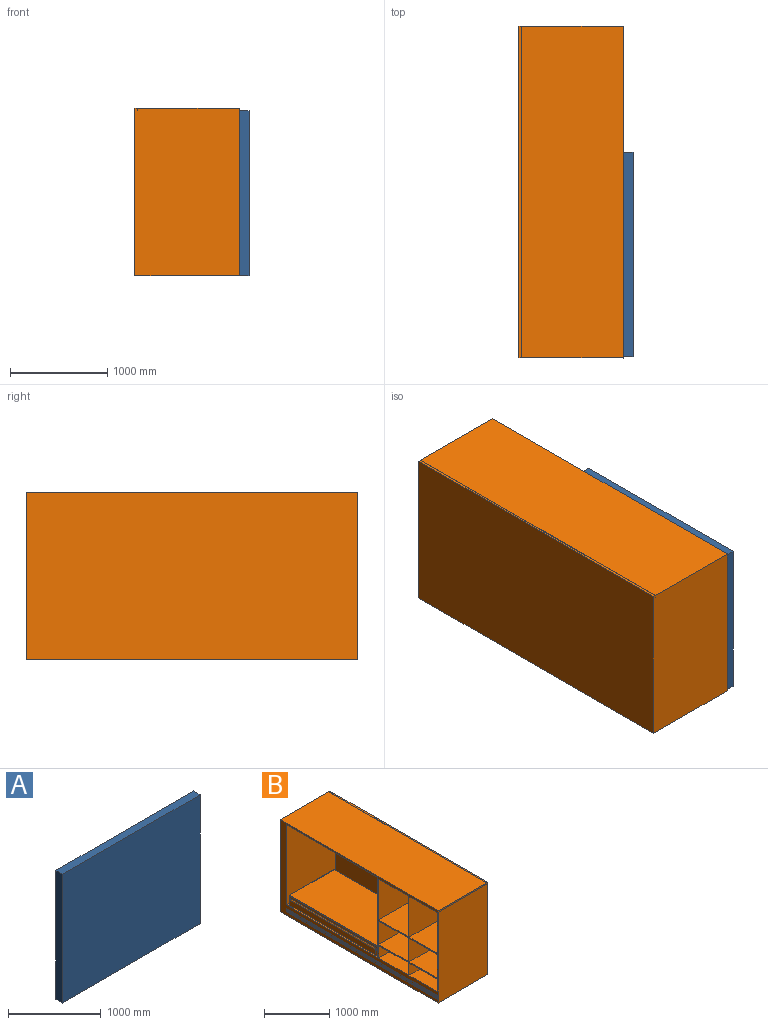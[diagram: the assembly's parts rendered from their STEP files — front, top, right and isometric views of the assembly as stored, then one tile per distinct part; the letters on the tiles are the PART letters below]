
ASSEMBLY  parts=2 mates=2
PART A: 6 faces, bbox 2100x100x1700 mm
  f0: plane 2100x1700mm, normal (0,1,0), area 3570000mm2, adj f1,f3,f4,f5
  f1: plane 1700x100mm, normal (-1,0,0), area 170000mm2, adj f0,f2,f4,f5
  f2: plane 2100x1700mm, normal (0,-1,0), area 3570000mm2, adj f1,f3,f4,f5
  f3: plane 1700x100mm, normal (1,0,0), area 170000mm2, adj f0,f2,f4,f5
  f4: plane 2100x100mm, normal (0,0,1), area 210000mm2, adj f0,f1,f2,f3
  f5: plane 2100x100mm, normal (0,0,-1), area 210000mm2, adj f0,f1,f2,f3
PART B: 94 faces, bbox 1080x3415.1x1725 mm
  f0: plane 763.79x630mm, normal (-1,0,0), area 481187.5mm2, adj f71,f73,f74,f93
  f1: plane 1019x763.79mm, normal (0,1,0), area 775969.2mm2, adj f2,f13,f79,f84,f90
  f2: plane 763.79x610mm, normal (-1,0,0), area 465911.7mm2, adj f1,f76,f79,f90
  f3: plane 1019x441.31mm, normal (0,-1,0), area 449692.9mm2, adj f6,f13,f88,f92
  f4: plane 1019x441.31mm, normal (0,1,0), area 449692.9mm2, adj f6,f13,f88,f92
  f5: plane 1019x441.31mm, normal (0,-1,0), area 449692.9mm2, adj f8,f13,f86,f91
  f6: plane 630x441.31mm, normal (-1,0,0), area 278024.1mm2, adj f3,f4,f88,f92
  f7: plane 1019x441.31mm, normal (0,1,0), area 449692.9mm2, adj f8,f13,f86,f91
  f8: plane 610x441.31mm, normal (-1,0,0), area 269197.9mm2, adj f5,f7,f86,f91
  f9: plane 1019x232.38mm, normal (0,-1,0), area 236797.7mm2, adj f13,f72,f75,f89
  f10: plane 1019x232.38mm, normal (0,1,0), area 236797.7mm2, adj f13,f72,f75,f89
  f11: plane 1019x232.38mm, normal (0,-1,0), area 236797.7mm2, adj f13,f77,f80,f87
  f12: plane 137x1.45mm, normal (0,0,1), area 198.3mm2, adj f15,f19,f20,f83
  f13: plane 3415.14x1725mm, normal (-1,0,0), area 1088941.3mm2, adj f1,f3,f4,f5,f7,f9,f10,f11
  f14: plane 3415.14x1075mm, normal (0,0,-1), area 3671270.9mm2, adj f13,f18,f69,f83
  f15: plane 3414.78x25mm, normal (1,0,0), area 85369.5mm2, adj f12,f16,f21,f81,f82,f83
  f16: plane 3414.78x1048.55mm, normal (0,0,1), area 3580578.9mm2, adj f13,f15,f81,f83
  f17: plane 3415.14x25mm, normal (0,0,1), area 85378.4mm2, adj f18,f19,f69,f83
  f18: plane 3415.14x1724.51mm, normal (1,0,0), area 5889440.8mm2, adj f14,f17,f69,f83
  f19: plane 3415.14x1524.51mm, normal (-1,0,0), area 3050913.7mm2, adj f12,f17,f20,f21,f22,f69,f70,f83
  f20: plane 1500x1050mm, normal (0,-1,0), area 1575000mm2, adj f12,f13,f19,f22,f82
  f21: plane 1300x1050mm, normal (0,0,1), area 2252.7mm2, adj f13,f15,f19,f69,f70,f81
  f22: plane 1978.14x1050mm, normal (0,0,1), area 123979.4mm2, adj f13,f19,f20,f23,f24,f25,f26,f27
  f23: plane 1855.15x100mm, normal (-1,0,0), area 185514.7mm2, adj f22,f27,f30,f36
  f24: plane 905.15x100mm, normal (0,-1,0), area 90514.7mm2, adj f22,f27,f28,f37
  f25: plane 1855.15x100mm, normal (1,0,0), area 185514.7mm2, adj f22,f28,f29,f33
  f26: plane 905.15x100mm, normal (0,1,0), area 90514.7mm2, adj f22,f29,f30,f32
  f27: cylinder r=48.28mm len=100mm, axis (0,0,-1), area 7584.5mm2, adj f22,f23,f24,f38
  f28: cylinder r=48.28mm len=100mm, axis (0,0,1), area 7584.5mm2, adj f22,f24,f25,f35
  f29: cylinder r=48.28mm len=100mm, axis (0,0,-1), area 7584.5mm2, adj f22,f25,f26,f31
  f30: cylinder r=48.28mm len=100mm, axis (0,0,1), area 7584.5mm2, adj f22,f23,f26,f34
  f31: torus R=28.28mm, axis (0,0,1), area 2024.1mm2, adj f29,f32,f33,f39
  f32: cylinder r=20mm len=905.15mm, axis (1,0,0), area 28436mm2, adj f26,f31,f34,f39
  f33: cylinder r=20mm len=1855.15mm, axis (0,-1,0), area 58281.2mm2, adj f25,f31,f35,f39
  f34: torus R=28.28mm, axis (0,0,1), area 2024.1mm2, adj f30,f32,f36,f39
  f35: torus R=28.28mm, axis (0,0,1), area 2024.1mm2, adj f28,f33,f37,f39
  f36: cylinder r=20mm len=1855.15mm, axis (0,1,0), area 58281.2mm2, adj f23,f34,f38,f39
  f37: cylinder r=20mm len=905.15mm, axis (-1,0,0), area 28436mm2, adj f24,f35,f38,f39
  f38: torus R=28.28mm, axis (0,0,1), area 2024.1mm2, adj f27,f36,f37,f39
  f39: plane 1923.48x973.41mm, normal (0,0,-1), area 34400.8mm2, adj f31,f32,f33,f34,f35,f36,f37,f38
  f40: plane 1903.48x40mm, normal (-1,0,0), area 76139.3mm2, adj f39,f45,f48,f54
  f41: plane 953.41x40mm, normal (0,-1,0), area 38136.2mm2, adj f39,f45,f46,f55
  f42: plane 1903.48x40mm, normal (1,0,0), area 76139.3mm2, adj f39,f46,f47,f51
  f43: plane 953.41x40mm, normal (0,1,0), area 38136.2mm2, adj f39,f47,f48,f50
  f44: plane 1903.48x953.41mm, normal (0,0,1), area 1814789.2mm2, adj f50,f51,f54,f55
  f45: cylinder r=10mm len=40mm, axis (0,0,-1), area 628.3mm2, adj f39,f40,f41,f56
  f46: cylinder r=10mm len=40mm, axis (0,0,1), area 628.3mm2, adj f39,f41,f42,f53
  f47: cylinder r=10mm len=40mm, axis (0,0,-1), area 628.3mm2, adj f39,f42,f43,f49
  f48: cylinder r=10mm len=40mm, axis (0,0,1), area 628.3mm2, adj f39,f40,f43,f52
  f49: sphere r=10mm, area 157.1mm2, adj f47,f50,f51
  f50: cylinder r=10mm len=953.41mm, axis (1,0,0), area 14976.1mm2, adj f43,f44,f49,f52
  f51: cylinder r=10mm len=1903.48mm, axis (0,-1,0), area 29899.8mm2, adj f42,f44,f49,f53
  f52: sphere r=10mm, area 157.1mm2, adj f48,f50,f54
  f53: sphere r=10mm, area 157.1mm2, adj f46,f51,f55
  f54: cylinder r=10mm len=1903.48mm, axis (0,1,0), area 29899.8mm2, adj f40,f44,f52,f56
  f55: cylinder r=10mm len=953.41mm, axis (-1,0,0), area 14976.1mm2, adj f41,f44,f53,f56
  f56: sphere r=10mm, area 157.1mm2, adj f45,f54,f55
  f57: plane 3280x5mm, normal (0,0,1), area 16400mm2, adj f13,f58,f60,f69
  f58: plane 5x5mm, normal (0,1,0), area 25mm2, adj f13,f57,f59,f60
  f59: plane 3280x5mm, normal (0,0,-1), area 16400mm2, adj f13,f58,f60,f69
  f60: plane 3280x5mm, normal (-1,0,0), area 16400mm2, adj f57,f58,f59,f69
  f61: plane 3280x5mm, normal (0,0,-1), area 16400mm2, adj f13,f63,f64,f69
  f62: plane 3280x5mm, normal (0,0,1), area 16400mm2, adj f13,f63,f64,f69
  f63: plane 5x5mm, normal (0,1,0), area 25mm2, adj f13,f61,f62,f64
  f64: plane 3280x5mm, normal (-1,0,0), area 16400mm2, adj f61,f62,f63,f69
  f65: plane 3280x5mm, normal (0,0,1), area 16400mm2, adj f13,f66,f68,f69
  f66: plane 6x5mm, normal (0,1,0), area 30mm2, adj f13,f65,f67,f68
  f67: plane 3280x5mm, normal (0,0,-1), area 16400mm2, adj f13,f66,f68,f69
  f68: plane 3280x6mm, normal (-1,0,0), area 19680mm2, adj f65,f66,f67,f69
  f69: plane 1724.51x1080mm, normal (0,-1,0), area 1828192.8mm2, adj f13,f14,f17,f18,f19,f21,f57,f59
  f70: plane 1500x1050mm, normal (0,1,0), area 1575000mm2, adj f13,f19,f21,f22,f82
  f71: plane 1019x763.79mm, normal (0,-1,0), area 775969.2mm2, adj f0,f13,f74,f85,f93
  f72: plane 1019x630mm, normal (0,0,1), area 641970mm2, adj f9,f10,f13,f75
  f73: plane 1019x763.79mm, normal (0,1,0), area 775969.2mm2, adj f0,f13,f74,f85,f93
  f74: plane 1019x630mm, normal (0,0,-1), area 641970mm2, adj f0,f13,f71,f73
  f75: plane 630x232.38mm, normal (-1,0,0), area 146400.9mm2, adj f9,f10,f72,f89
  f76: plane 1019x763.79mm, normal (0,-1,0), area 775969.2mm2, adj f2,f13,f79,f84,f90
  f77: plane 1019x610mm, normal (0,0,1), area 621590mm2, adj f11,f13,f78,f80
  f78: plane 1019x232.38mm, normal (0,1,0), area 236797.7mm2, adj f13,f77,f80,f87
  f79: plane 1019x610mm, normal (0,0,-1), area 621590mm2, adj f1,f2,f13,f76
  f80: plane 610x232.38mm, normal (-1,0,0), area 141753.3mm2, adj f11,f77,f78,f87
  f81: plane 1048.55x25mm, normal (0,-1,0), area 26213.8mm2, adj f13,f15,f16,f21
  f82: plane 1978.14x1048.55mm, normal (0,0,-1), area 2074179.9mm2, adj f13,f15,f20,f70
  f83: plane 1725x1075mm, normal (0,1,0), area 1854326.6mm2, adj f12,f13,f14,f15,f16,f17,f18,f19
  f84: cylinder r=27.25mm len=610mm, axis (0,-1,0), area 104433.6mm2, adj f1,f76
  f85: cylinder r=27.25mm len=630mm, axis (0,-1,0), area 107857.7mm2, adj f71,f73
  f86: plane 1019x610mm, normal (0,0,1), area 621590mm2, adj f5,f7,f8,f13
  f87: plane 1019x610mm, normal (0,0,-1), area 621590mm2, adj f11,f13,f78,f80
  f88: plane 1019x630mm, normal (0,0,1), area 641970mm2, adj f3,f4,f6,f13
  f89: plane 1019x630mm, normal (0,0,-1), area 641970mm2, adj f9,f10,f13,f75
  f90: plane 1019x610mm, normal (0,0,1), area 621590mm2, adj f1,f2,f13,f76
  f91: plane 1019x610mm, normal (0,0,-1), area 621590mm2, adj f5,f7,f8,f13
  f92: plane 1019x630mm, normal (0,0,-1), area 641970mm2, adj f3,f4,f6,f13
  f93: plane 1019x630mm, normal (0,0,1), area 641970mm2, adj f0,f13,f71,f73
PLACE A rot(axis=(0,0,-1),90deg) t=(-2713.96,877.02,429)mm
PLACE B rot(axis=(0,0,-1),180deg) t=(-2722.15,942.08,429)mm
MATE slider A.f1 <-> B.f70  axis (0,1,0) through (-2622.15,942.08,2129)mm
MATE slider A.f3 <-> A.f3  axis (0,-1,0) through (-2622.15,-1157.92,429)mm
